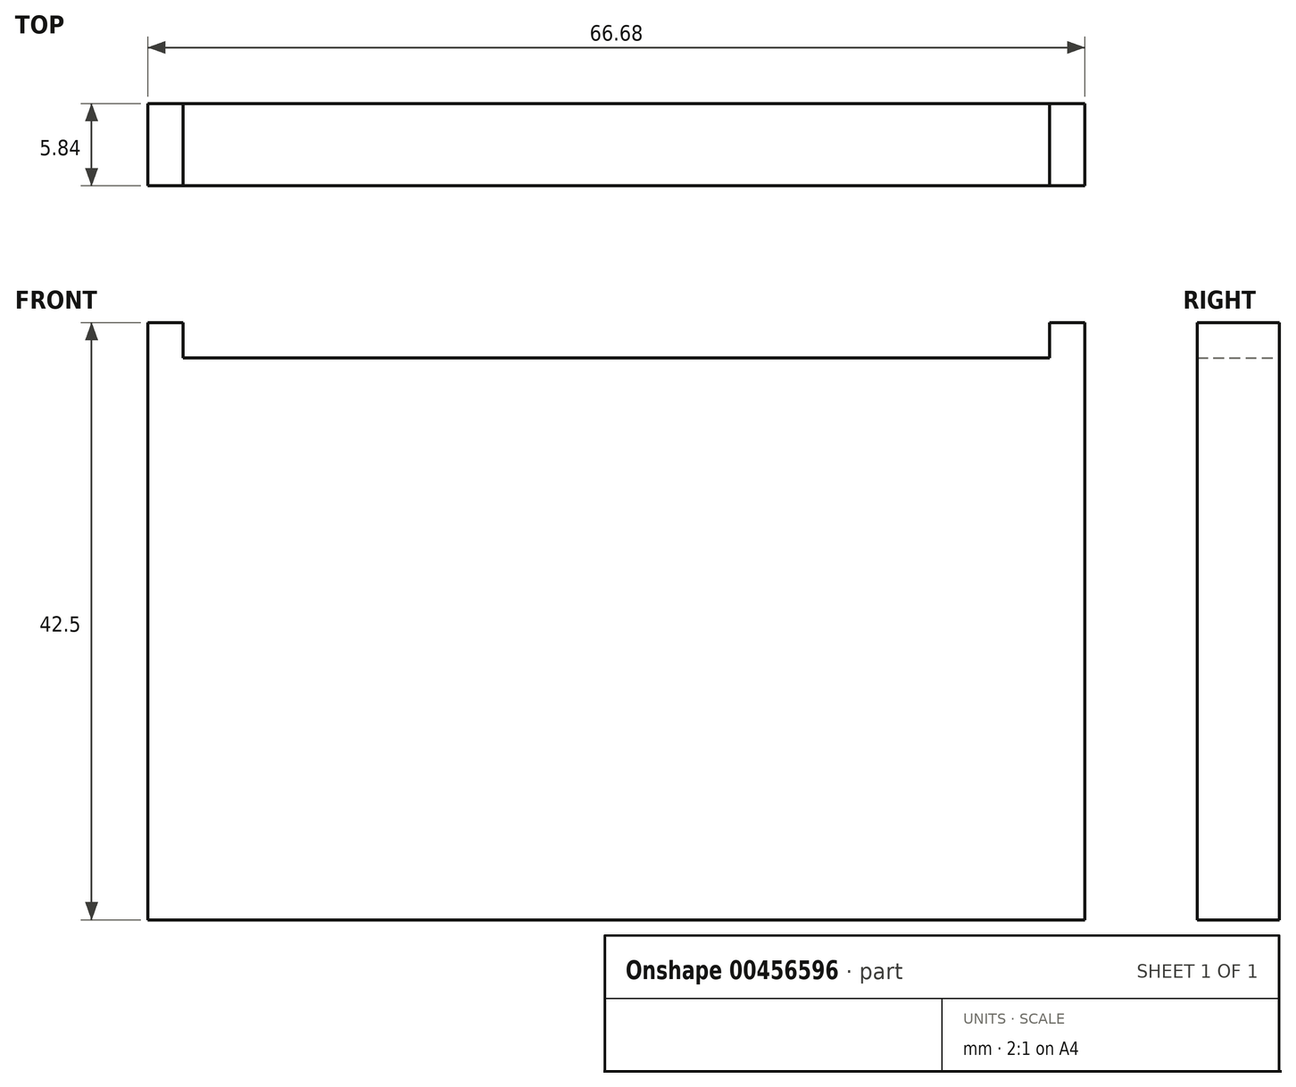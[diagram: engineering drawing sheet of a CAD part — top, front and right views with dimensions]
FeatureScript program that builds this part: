
annotation { "Feature Type Name" : "Feature", "Feature Type Description" : "" }
export const myFeature = defineFeature(function(context is Context, id is Id, definition is map)
    precondition{}
    {
        {
            var Q0;
            Q0=qCreatedBy(makeId("Front.planeOp"),FACE);
            var sketch = newSketch(context, id + "F0", { "sketchPlane" : qUnion([Q0])});
            skLineSegment(sketch, "E0.bottom", {"start": v(33.34, 21.25) * mm, "end": v(30.84, 21.25) * mm});
            skLineSegment(sketch, "E0.top", {"start": v(33.34, -21.25) * mm, "end": v(-33.34, -21.25) * mm});
            skLineSegment(sketch, "E0.left", {"start": v(33.34, 21.25) * mm, "end": v(33.34, -21.25) * mm});
            skLineSegment(sketch, "E0.right", {"start": v(-33.34, 21.25) * mm, "end": v(-33.34, -21.25) * mm});
            skPoint(sketch, "E0.middle", {"position": v(0, 0) * mm});
            skLineSegment(sketch, "E1.top", {"start": v(30.84, 18.75) * mm, "end": v(-30.84, 18.75) * mm});
            skLineSegment(sketch, "E1.left", {"start": v(30.84, 21.25) * mm, "end": v(30.84, 18.75) * mm});
            skLineSegment(sketch, "E1.right", {"start": v(-30.84, 21.25) * mm, "end": v(-30.84, 18.75) * mm});
            skPoint(sketch, "E1.middle", {"position": v(0, 21.25) * mm});
            skLineSegment(sketch, "E2.trimOffspring", {"start": v(-30.84, 21.25) * mm, "end": v(-33.34, 21.25) * mm});
            skPoint(sketch, "E3.orphan", {"position": v(-30.84, 23.75) * mm});
            skPoint(sketch, "E4.orphan", {"position": v(30.84, 23.75) * mm});
            skSolve(sketch);
        }
        {
            var Q0;
            Q0 = qSketchRegion(id + "F0", true);
            extrude(context, id + "F1", {"entities" : qUnion([Q0]), "depth" : 5.84 * mm});
        }
    });
